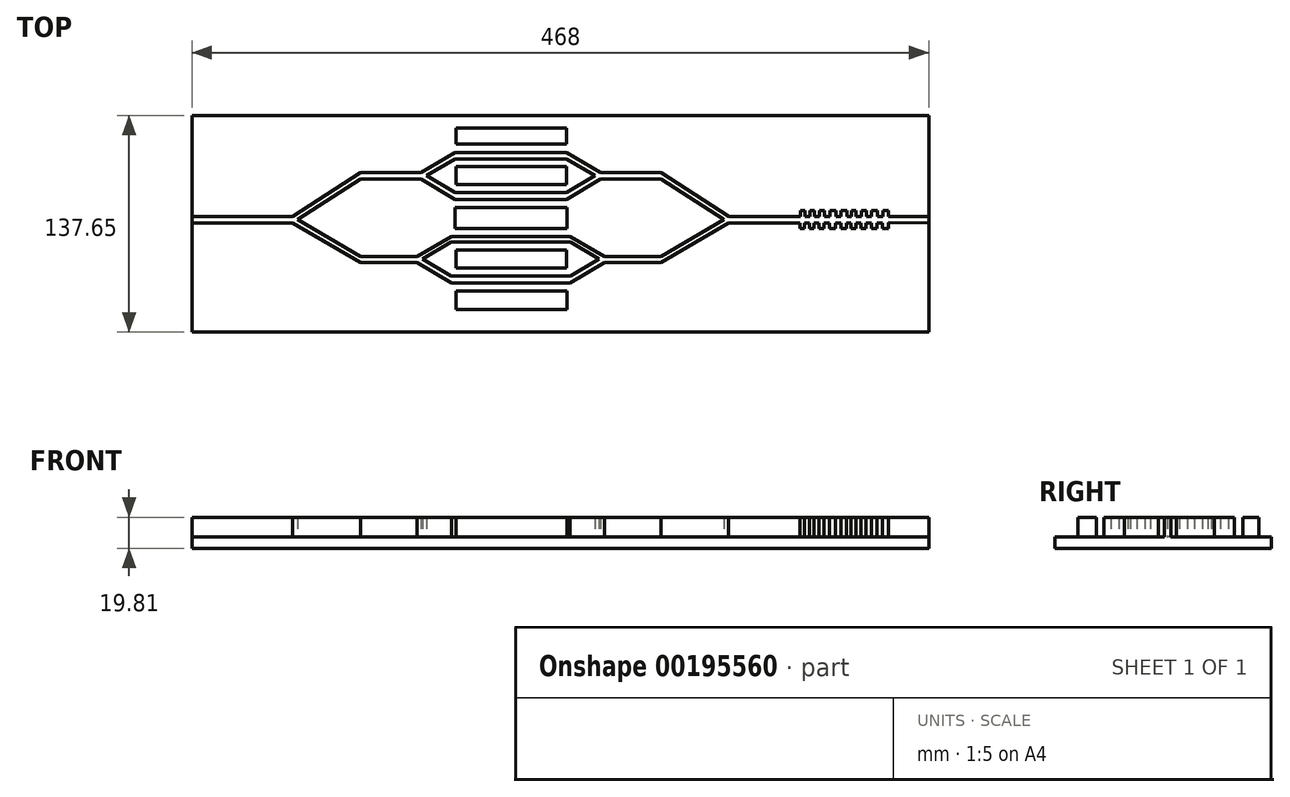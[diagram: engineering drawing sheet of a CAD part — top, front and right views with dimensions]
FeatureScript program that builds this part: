
annotation { "Feature Type Name" : "Feature", "Feature Type Description" : "" }
export const myFeature = defineFeature(function(context is Context, id is Id, definition is map)
    precondition{}
    {
        {
            var Q0;
            Q0=qCreatedBy(makeId("Top.planeOp"),FACE);
            var sketch = newSketch(context, id + "F0", { "sketchPlane" : qUnion([Q0])});
            skLineSegment(sketch, "E0.bottom", {"start": v(-202.47, -68.03) * mm, "end": v(265.53, -68.03) * mm});
            skLineSegment(sketch, "E0.top", {"start": v(-202.47, 69.62) * mm, "end": v(265.53, 69.62) * mm});
            skLineSegment(sketch, "E0.left", {"start": v(-202.47, -68.03) * mm, "end": v(-202.47, 69.62) * mm});
            skLineSegment(sketch, "E0.right", {"start": v(265.53, -68.03) * mm, "end": v(265.53, 69.62) * mm});
            skSolve(sketch);
        }
        {
            var Q0;
            Q0 = qSketchRegion(id + "F0", true);
            extrude(context, id + "F1", {"entities" : qUnion([Q0]), "depth" : 7.37 * mm});
        }
        {
            var Q0;
            Q0=makeQuery(id+"F1.opExtrude","CAP_FACE",FACE,{"disambiguationData":[OSD([sQuery(id+"F0.wireOp",EDGE,"E0.bottom"),sQuery(id+"F0.wireOp",EDGE,"E0.top"),sQuery(id+"F0.wireOp",EDGE,"E0.left"),sQuery(id+"F0.wireOp",EDGE,"E0.right")])],"isStart":false});
            var sketch = newSketch(context, id + "F2", { "sketchPlane" : qUnion([Q0])});
            skLineSegment(sketch, "E1.bottom", {"start": v(-156.35, 5.45) * mm, "end": v(-138.65, 5.45) * mm});
            skLineSegment(sketch, "E1.top", {"start": v(-156.6, 1.4) * mm, "end": v(-138.42, 1.4) * mm});
            skLineSegment(sketch, "E2", {"start": v(-138.65, 5.45) * mm, "end": v(-95.28, 33.3) * mm});
            skLineSegment(sketch, "E3.MirrorCS", {"start": v(-138.42, 1.4) * mm, "end": v(-95.29, -23.79) * mm});
            skLineSegment(sketch, "E4", {"start": v(-95.29, 29.2) * mm, "end": v(-135.34, 3.48) * mm});
            skLineSegment(sketch, "E5", {"start": v(-95.29, -19.91) * mm, "end": v(-135.34, 3.48) * mm});
            skLineSegment(sketch, "E6", {"start": v(-95.28, 33.3) * mm, "end": v(-57.06, 33.3) * mm});
            skLineSegment(sketch, "E7", {"start": v(-95.29, 29.2) * mm, "end": v(-57.06, 29.2) * mm});
            skLineSegment(sketch, "E8", {"start": v(-95.29, -19.91) * mm, "end": v(-59.46, -19.91) * mm});
            skLineSegment(sketch, "E9", {"start": v(-95.29, -23.79) * mm, "end": v(-59.46, -23.79) * mm});
            skLineSegment(sketch, "E10", {"start": v(-57.06, 33.3) * mm, "end": v(-35.34, 45.95) * mm});
            skLineSegment(sketch, "E11", {"start": v(-57.06, 29.2) * mm, "end": v(-35.34, 16.28) * mm});
            skLineSegment(sketch, "E12", {"start": v(-53.49, 31.34) * mm, "end": v(-35.36, 42.1) * mm});
            skLineSegment(sketch, "E13", {"start": v(-53.49, 31.34) * mm, "end": v(-35.36, 20.57) * mm});
            skLineSegment(sketch, "E14", {"start": v(-59.46, -19.91) * mm, "end": v(-37.74, -7.26) * mm});
            skLineSegment(sketch, "E15", {"start": v(-59.46, -23.79) * mm, "end": v(-37.74, -36.71) * mm});
            skLineSegment(sketch, "E16", {"start": v(-55.94, -21.59) * mm, "end": v(-37.81, -10.82) * mm});
            skLineSegment(sketch, "E17", {"start": v(-55.94, -21.59) * mm, "end": v(-37.81, -32.35) * mm});
            skLineSegment(sketch, "E18", {"start": v(-35.34, 45.95) * mm, "end": v(0, 45.95) * mm});
            skLineSegment(sketch, "E19", {"start": v(-35.36, 42.1) * mm, "end": v(0, 42.1) * mm});
            skLineSegment(sketch, "E20", {"start": v(-35.36, 20.57) * mm, "end": v(0, 20.57) * mm});
            skLineSegment(sketch, "E21", {"start": v(-35.34, 16.28) * mm, "end": v(0, 16.28) * mm});
            skLineSegment(sketch, "E22", {"start": v(-37.74, -7.26) * mm, "end": v(0, -7.26) * mm});
            skLineSegment(sketch, "E23", {"start": v(-37.81, -10.82) * mm, "end": v(0, -10.82) * mm});
            skLineSegment(sketch, "E24", {"start": v(-37.81, -32.35) * mm, "end": v(0, -32.35) * mm});
            skLineSegment(sketch, "E25", {"start": v(-37.74, -36.71) * mm, "end": v(0, -36.71) * mm});
            skLineSegment(sketch, "E26.MirrorCS", {"start": v(95.29, -19.91) * mm, "end": v(135.34, 3.48) * mm});
            skLineSegment(sketch, "E27.MirrorCS", {"start": v(95.28, 33.3) * mm, "end": v(57.06, 33.3) * mm});
            skLineSegment(sketch, "E28.MirrorCS", {"start": v(95.29, 29.2) * mm, "end": v(135.34, 3.48) * mm});
            skLineSegment(sketch, "E29.MirrorCS", {"start": v(138.42, 1.4) * mm, "end": v(95.29, -23.79) * mm});
            skLineSegment(sketch, "E30.MirrorCS", {"start": v(37.74, -7.26) * mm, "end": v(0, -7.26) * mm});
            skLineSegment(sketch, "E31.MirrorCS", {"start": v(95.29, 29.2) * mm, "end": v(57.06, 29.2) * mm});
            skLineSegment(sketch, "E32.MirrorCS", {"start": v(95.29, -19.91) * mm, "end": v(59.46, -19.91) * mm});
            skLineSegment(sketch, "E33.MirrorCS", {"start": v(138.65, 5.45) * mm, "end": v(95.28, 33.3) * mm});
            skLineSegment(sketch, "E34.MirrorCS", {"start": v(55.94, -21.59) * mm, "end": v(37.81, -32.35) * mm});
            skLineSegment(sketch, "E35.MirrorCS", {"start": v(37.81, -10.82) * mm, "end": v(0, -10.82) * mm});
            skLineSegment(sketch, "E36.MirrorCS", {"start": v(53.49, 31.34) * mm, "end": v(35.36, 20.57) * mm});
            skLineSegment(sketch, "E37.MirrorCS", {"start": v(35.36, 42.1) * mm, "end": v(0, 42.1) * mm});
            skLineSegment(sketch, "E38.MirrorCS", {"start": v(35.34, 45.95) * mm, "end": v(0, 45.95) * mm});
            skLineSegment(sketch, "E39.MirrorCS", {"start": v(95.29, -23.79) * mm, "end": v(59.46, -23.79) * mm});
            skLineSegment(sketch, "E40.MirrorCS", {"start": v(55.94, -21.59) * mm, "end": v(37.81, -10.82) * mm});
            skLineSegment(sketch, "E41.MirrorCS", {"start": v(37.74, -36.71) * mm, "end": v(0, -36.71) * mm});
            skLineSegment(sketch, "E42.MirrorCS", {"start": v(59.46, -19.91) * mm, "end": v(37.74, -7.26) * mm});
            skLineSegment(sketch, "E43.MirrorCS", {"start": v(57.06, 33.3) * mm, "end": v(35.34, 45.95) * mm});
            skLineSegment(sketch, "E44.MirrorCS", {"start": v(35.36, 20.57) * mm, "end": v(0, 20.57) * mm});
            skLineSegment(sketch, "E45.MirrorCS", {"start": v(156.6, 1.4) * mm, "end": v(138.42, 1.4) * mm});
            skLineSegment(sketch, "E46.MirrorCS", {"start": v(57.06, 29.2) * mm, "end": v(35.34, 16.28) * mm});
            skLineSegment(sketch, "E47.MirrorCS", {"start": v(156.35, 5.45) * mm, "end": v(138.65, 5.45) * mm});
            skLineSegment(sketch, "E48.MirrorCS", {"start": v(59.46, -23.79) * mm, "end": v(37.74, -36.71) * mm});
            skLineSegment(sketch, "E49.MirrorCS", {"start": v(37.81, -32.35) * mm, "end": v(0, -32.35) * mm});
            skLineSegment(sketch, "E50.MirrorCS", {"start": v(35.34, 16.28) * mm, "end": v(0, 16.28) * mm});
            skLineSegment(sketch, "E51.MirrorCS", {"start": v(53.49, 31.34) * mm, "end": v(35.36, 42.1) * mm});
            skLineSegment(sketch, "E52", {"start": v(156.35, 5.45) * mm, "end": v(181.75, 5.45) * mm});
            skLineSegment(sketch, "E53", {"start": v(156.6, 1.4) * mm, "end": v(181.73, 1.4) * mm});
            skLineSegment(sketch, "E54", {"start": v(183.86, 5.45) * mm, "end": v(183.86, 9.35) * mm});
            skLineSegment(sketch, "E55", {"start": v(183.86, 9.35) * mm, "end": v(186.92, 9.35) * mm});
            skLineSegment(sketch, "E56", {"start": v(186.92, 9.35) * mm, "end": v(186.92, 5.6) * mm});
            skLineSegment(sketch, "E57", {"start": v(186.92, 5.6) * mm, "end": v(189.9, 5.6) * mm});
            skLineSegment(sketch, "E58", {"start": v(189.9, 5.6) * mm, "end": v(189.9, 9.35) * mm});
            skLineSegment(sketch, "E59", {"start": v(189.9, 9.35) * mm, "end": v(192.9, 9.35) * mm});
            skLineSegment(sketch, "E60", {"start": v(192.9, 9.35) * mm, "end": v(192.9, 5.6) * mm});
            skLineSegment(sketch, "E61", {"start": v(192.9, 5.6) * mm, "end": v(196.13, 5.6) * mm});
            skLineSegment(sketch, "E62", {"start": v(196.13, 5.6) * mm, "end": v(196.13, 9.35) * mm});
            skLineSegment(sketch, "E63", {"start": v(196.13, 9.35) * mm, "end": v(199.35, 9.35) * mm});
            skLineSegment(sketch, "E64", {"start": v(199.35, 9.35) * mm, "end": v(199.35, 5.6) * mm});
            skLineSegment(sketch, "E65", {"start": v(199.35, 5.6) * mm, "end": v(202.73, 5.6) * mm});
            skLineSegment(sketch, "E66", {"start": v(202.73, 5.6) * mm, "end": v(202.73, 9.35) * mm});
            skLineSegment(sketch, "E67", {"start": v(202.73, 9.35) * mm, "end": v(206.5, 9.35) * mm});
            skLineSegment(sketch, "E68", {"start": v(206.5, 9.35) * mm, "end": v(206.5, 5.6) * mm});
            skLineSegment(sketch, "E69", {"start": v(206.5, 5.6) * mm, "end": v(209.87, 5.6) * mm});
            skLineSegment(sketch, "E70", {"start": v(209.87, 5.6) * mm, "end": v(209.87, 9.35) * mm});
            skLineSegment(sketch, "E71", {"start": v(209.87, 9.35) * mm, "end": v(213.4, 9.35) * mm});
            skLineSegment(sketch, "E72", {"start": v(213.4, 9.35) * mm, "end": v(213.4, 5.6) * mm});
            skLineSegment(sketch, "E73.MirrorCS", {"start": v(186.66, -2.29) * mm, "end": v(186.66, 1.48) * mm});
            skLineSegment(sketch, "E74.MirrorCS", {"start": v(199.1, 1.48) * mm, "end": v(202.48, 1.48) * mm});
            skLineSegment(sketch, "E75.MirrorCS", {"start": v(199.1, -2.29) * mm, "end": v(199.1, 1.48) * mm});
            skLineSegment(sketch, "E76.MirrorCS", {"start": v(189.66, 1.48) * mm, "end": v(189.66, -2.29) * mm});
            skLineSegment(sketch, "E77.MirrorCS", {"start": v(186.66, 1.48) * mm, "end": v(189.66, 1.48) * mm});
            skLineSegment(sketch, "E78.MirrorCS", {"start": v(202.48, 1.48) * mm, "end": v(202.48, -2.29) * mm});
            skLineSegment(sketch, "E79.MirrorCS", {"start": v(189.66, -2.29) * mm, "end": v(192.65, -2.29) * mm});
            skLineSegment(sketch, "E80.MirrorCS", {"start": v(202.48, -2.29) * mm, "end": v(206.24, -2.29) * mm});
            skLineSegment(sketch, "E81.MirrorCS", {"start": v(192.65, -2.29) * mm, "end": v(192.65, 1.48) * mm});
            skLineSegment(sketch, "E82.MirrorCS", {"start": v(192.65, 1.48) * mm, "end": v(195.87, 1.48) * mm});
            skLineSegment(sketch, "E83.MirrorCS", {"start": v(206.24, -2.29) * mm, "end": v(206.24, 1.48) * mm});
            skLineSegment(sketch, "E84.MirrorCS", {"start": v(195.87, 1.48) * mm, "end": v(195.87, -2.29) * mm});
            skLineSegment(sketch, "E85.MirrorCS", {"start": v(183.6, -2.29) * mm, "end": v(186.66, -2.29) * mm});
            skLineSegment(sketch, "E86.MirrorCS", {"start": v(206.24, 1.48) * mm, "end": v(209.62, 1.48) * mm});
            skLineSegment(sketch, "E87.MirrorCS", {"start": v(209.62, 1.48) * mm, "end": v(209.62, -2.29) * mm});
            skLineSegment(sketch, "E88.MirrorCS", {"start": v(195.87, -2.29) * mm, "end": v(199.1, -2.29) * mm});
            skLineSegment(sketch, "E89.MirrorCS", {"start": v(209.62, -2.29) * mm, "end": v(213.15, -2.29) * mm});
            skLineSegment(sketch, "E90.MirrorCS", {"start": v(183.61, 1.4) * mm, "end": v(183.6, -2.29) * mm});
            skLineSegment(sketch, "E91.MirrorCS", {"start": v(213.15, -2.29) * mm, "end": v(213.15, 1.48) * mm});
            skLineSegment(sketch, "E92", {"start": v(213.4, 5.6) * mm, "end": v(216.4, 5.6) * mm});
            skLineSegment(sketch, "E93", {"start": v(216.4, 5.6) * mm, "end": v(216.4, 9.35) * mm});
            skLineSegment(sketch, "E94", {"start": v(216.4, 9.35) * mm, "end": v(219.39, 9.35) * mm});
            skLineSegment(sketch, "E95", {"start": v(219.39, 9.35) * mm, "end": v(219.39, 5.6) * mm});
            skLineSegment(sketch, "E96", {"start": v(219.39, 5.6) * mm, "end": v(222.61, 5.6) * mm});
            skLineSegment(sketch, "E97", {"start": v(222.61, 5.6) * mm, "end": v(222.61, 9.35) * mm});
            skLineSegment(sketch, "E98", {"start": v(222.61, 9.35) * mm, "end": v(225.84, 9.35) * mm});
            skLineSegment(sketch, "E99", {"start": v(225.84, 9.35) * mm, "end": v(225.84, 5.6) * mm});
            skLineSegment(sketch, "E100", {"start": v(225.84, 5.6) * mm, "end": v(229.22, 5.6) * mm});
            skLineSegment(sketch, "E101", {"start": v(229.22, 5.6) * mm, "end": v(229.22, 9.35) * mm});
            skLineSegment(sketch, "E102", {"start": v(229.22, 9.35) * mm, "end": v(232.98, 9.35) * mm});
            skLineSegment(sketch, "E103", {"start": v(232.98, 9.35) * mm, "end": v(232.98, 5.6) * mm});
            skLineSegment(sketch, "E104", {"start": v(232.98, 5.6) * mm, "end": v(236.36, 5.6) * mm});
            skLineSegment(sketch, "E105", {"start": v(236.36, 5.6) * mm, "end": v(236.36, 9.35) * mm});
            skLineSegment(sketch, "E106", {"start": v(236.36, 9.35) * mm, "end": v(239.89, 9.35) * mm});
            skLineSegment(sketch, "E107", {"start": v(239.89, 9.35) * mm, "end": v(239.89, 5.6) * mm});
            skLineSegment(sketch, "E108.MirrorCS", {"start": v(225.58, 1.48) * mm, "end": v(228.96, 1.48) * mm});
            skLineSegment(sketch, "E109.MirrorCS", {"start": v(225.58, -2.29) * mm, "end": v(225.58, 1.48) * mm});
            skLineSegment(sketch, "E110.MirrorCS", {"start": v(216.14, 1.48) * mm, "end": v(216.14, -2.29) * mm});
            skLineSegment(sketch, "E111.MirrorCS", {"start": v(213.15, 1.48) * mm, "end": v(216.14, 1.48) * mm});
            skLineSegment(sketch, "E112.MirrorCS", {"start": v(228.96, 1.48) * mm, "end": v(228.96, -2.29) * mm});
            skLineSegment(sketch, "E113.MirrorCS", {"start": v(216.14, -2.29) * mm, "end": v(219.14, -2.29) * mm});
            skLineSegment(sketch, "E114.MirrorCS", {"start": v(228.96, -2.29) * mm, "end": v(232.72, -2.29) * mm});
            skLineSegment(sketch, "E115.MirrorCS", {"start": v(219.14, -2.29) * mm, "end": v(219.14, 1.48) * mm});
            skLineSegment(sketch, "E116.MirrorCS", {"start": v(219.14, 1.48) * mm, "end": v(222.36, 1.48) * mm});
            skLineSegment(sketch, "E117.MirrorCS", {"start": v(232.72, -2.29) * mm, "end": v(232.72, 1.48) * mm});
            skLineSegment(sketch, "E118.MirrorCS", {"start": v(222.36, 1.48) * mm, "end": v(222.36, -2.29) * mm});
            skLineSegment(sketch, "E119.MirrorCS", {"start": v(232.72, 1.48) * mm, "end": v(236.1, 1.48) * mm});
            skLineSegment(sketch, "E120.MirrorCS", {"start": v(236.1, 1.48) * mm, "end": v(236.1, -2.29) * mm});
            skLineSegment(sketch, "E121.MirrorCS", {"start": v(222.36, -2.29) * mm, "end": v(225.58, -2.29) * mm});
            skLineSegment(sketch, "E122.MirrorCS", {"start": v(236.1, -2.29) * mm, "end": v(239.89, -2.29) * mm});
            skLineSegment(sketch, "E123.MirrorCS", {"start": v(239.89, -2.29) * mm, "end": v(239.89, 1.52) * mm});
            skLineSegment(sketch, "E124", {"start": v(183.86, 5.45) * mm, "end": v(181.75, 5.45) * mm});
            skLineSegment(sketch, "E125", {"start": v(183.61, 1.4) * mm, "end": v(181.73, 1.4) * mm});
            skLineSegment(sketch, "E126", {"start": v(239.89, 5.6) * mm, "end": v(265.53, 5.6) * mm});
            skLineSegment(sketch, "E127", {"start": v(265.53, 5.6) * mm, "end": v(265.53, 1.47) * mm});
            skLineSegment(sketch, "E128", {"start": v(265.53, 1.47) * mm, "end": v(239.89, 1.52) * mm});
            skLineSegment(sketch, "E129", {"start": v(-156.35, 5.45) * mm, "end": v(-202.47, 5.45) * mm});
            skLineSegment(sketch, "E130", {"start": v(-156.6, 1.4) * mm, "end": v(-202.47, 1.4) * mm});
            skLineSegment(sketch, "E131", {"start": v(-202.47, 1.4) * mm, "end": v(-202.47, 5.45) * mm});
            skLineSegment(sketch, "E132.bottom", {"start": v(-34.86, 37.06) * mm, "end": v(35.38, 37.06) * mm});
            skLineSegment(sketch, "E132.top", {"start": v(-34.86, 25.76) * mm, "end": v(35.38, 25.76) * mm});
            skLineSegment(sketch, "E132.left", {"start": v(-34.86, 37.06) * mm, "end": v(-34.86, 25.76) * mm});
            skLineSegment(sketch, "E132.right", {"start": v(35.38, 37.06) * mm, "end": v(35.38, 25.76) * mm});
            skLineSegment(sketch, "E133.bottom", {"start": v(-34.88, -15.89) * mm, "end": v(35.37, -15.89) * mm});
            skLineSegment(sketch, "E133.top", {"start": v(-34.88, -27.19) * mm, "end": v(35.37, -27.19) * mm});
            skLineSegment(sketch, "E133.left", {"start": v(-34.88, -15.89) * mm, "end": v(-34.88, -27.19) * mm});
            skLineSegment(sketch, "E133.right", {"start": v(35.37, -15.89) * mm, "end": v(35.37, -27.19) * mm});
            skLineSegment(sketch, "E134.bottom", {"start": v(-34.82, 61.76) * mm, "end": v(35.43, 61.76) * mm});
            skLineSegment(sketch, "E134.top", {"start": v(-34.82, 51.34) * mm, "end": v(35.43, 51.34) * mm});
            skLineSegment(sketch, "E134.left", {"start": v(-34.82, 61.76) * mm, "end": v(-34.82, 51.34) * mm});
            skLineSegment(sketch, "E134.right", {"start": v(35.43, 61.76) * mm, "end": v(35.43, 51.34) * mm});
            skLineSegment(sketch, "E135.bottom", {"start": v(-35.26, 11.01) * mm, "end": v(35.65, 11.01) * mm});
            skLineSegment(sketch, "E135.top", {"start": v(-35.26, -2.06) * mm, "end": v(35.65, -2.06) * mm});
            skLineSegment(sketch, "E135.left", {"start": v(-35.26, 11.01) * mm, "end": v(-35.26, -2.06) * mm});
            skLineSegment(sketch, "E135.right", {"start": v(35.65, 11.01) * mm, "end": v(35.65, -2.06) * mm});
            skLineSegment(sketch, "E136.bottom", {"start": v(-34.82, -41.73) * mm, "end": v(35.65, -41.73) * mm});
            skLineSegment(sketch, "E136.top", {"start": v(-34.82, -53.47) * mm, "end": v(35.65, -53.47) * mm});
            skLineSegment(sketch, "E136.left", {"start": v(-34.82, -41.73) * mm, "end": v(-34.82, -53.47) * mm});
            skLineSegment(sketch, "E136.right", {"start": v(35.65, -41.73) * mm, "end": v(35.65, -53.47) * mm});
            skSolve(sketch);
        }
        {
            var Q0;
            Q0 = qSketchRegion(id + "F2", true);
            var Q1;
            Q1=makeQuery(id+"F2.imprint","IMPRINT",FACE,{"disambiguationData":[TD([[makeQuery(id+"F2.imprint","IMPRINT",EDGE,{"derivedFrom":sQuery(id+"F2.wireOp",EDGE,"E132.bottom")}),-1.0]])]});
            var Q2;
            Q2=makeQuery(id+"F2.imprint","IMPRINT",FACE,{"disambiguationData":[TD([[makeQuery(id+"F2.imprint","IMPRINT",EDGE,{"derivedFrom":sQuery(id+"F2.wireOp",EDGE,"E135.bottom")}),-1.0]])]});
            var Q3;
            Q3=makeQuery(id+"F2.imprint","IMPRINT",FACE,{"disambiguationData":[TD([[makeQuery(id+"F2.imprint","IMPRINT",EDGE,{"derivedFrom":sQuery(id+"F2.wireOp",EDGE,"E133.bottom")}),-1.0]])]});
            extrude(context, id + "F3", {"entities" : qUnion([Q0, Q1, Q2, Q3]), "operationType" : NewBodyOperationType.ADD, "depth" : 12.45 * mm});
        }
    });
